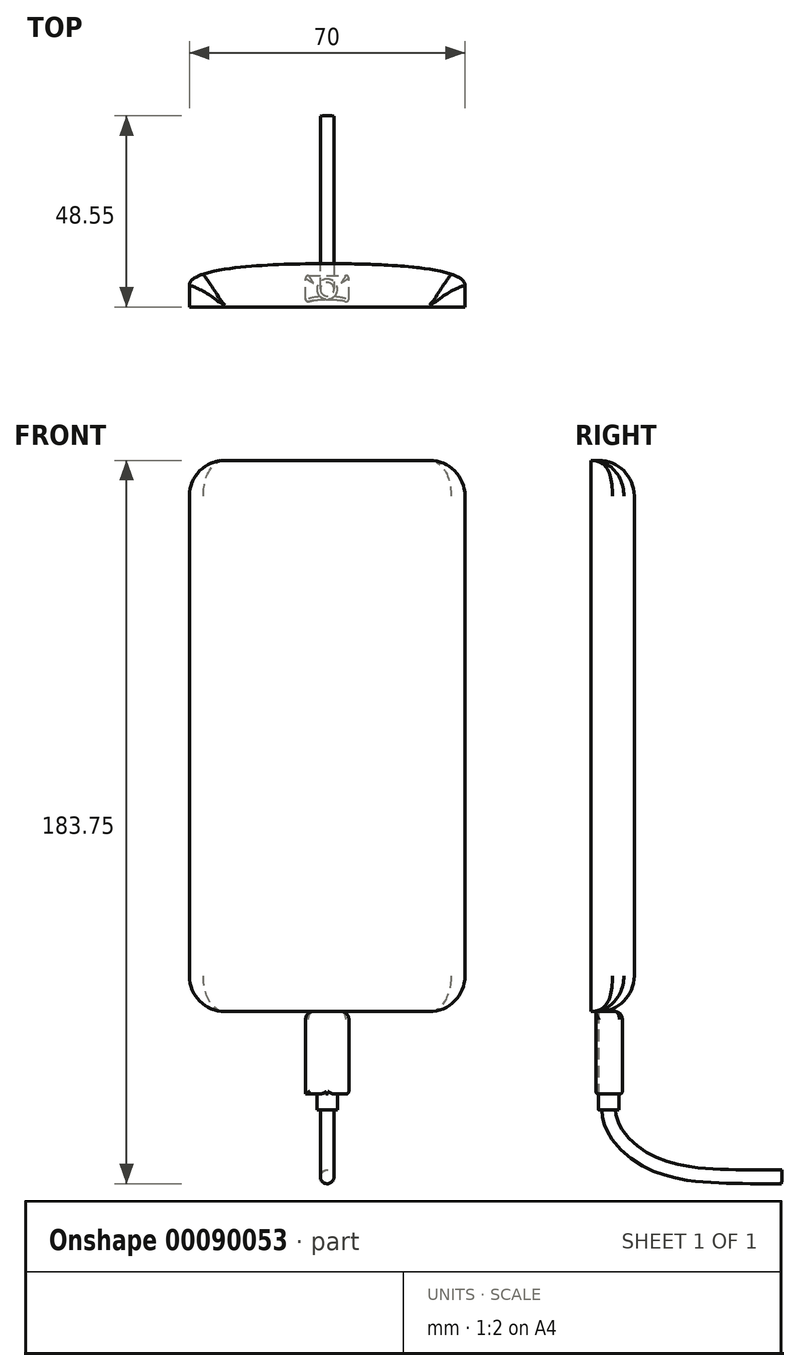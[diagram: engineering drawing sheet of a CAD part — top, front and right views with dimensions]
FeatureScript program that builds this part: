
annotation { "Feature Type Name" : "Feature", "Feature Type Description" : "" }
export const myFeature = defineFeature(function(context is Context, id is Id, definition is map)
    precondition{}
    {
        {
            var Q0;
            Q0=qCreatedBy(makeId("Front.planeOp"),FACE);
            var sketch = newSketch(context, id + "F0", { "sketchPlane" : qUnion([Q0])});
            skLineSegment(sketch, "E0.bottom", {"start": v(-35, 140) * mm, "end": v(35, 140) * mm});
            skLineSegment(sketch, "E0.top", {"start": v(-35, 0) * mm, "end": v(35, 0) * mm});
            skLineSegment(sketch, "E0.left", {"start": v(-35, 140) * mm, "end": v(-35, 0) * mm});
            skLineSegment(sketch, "E0.right", {"start": v(35, 140) * mm, "end": v(35, 0) * mm});
            skSolve(sketch);
        }
        {
            var Q0;
            Q0=qSketchRegion(id+"F0",true);
            extrude(context, id + "F1", {"entities" : qUnion([Q0]), "depth" : 11 * mm});
        }
        {
            var Q0;
            Q0=makeQuery(id+"F1.opExtrude","SWEPT_FACE",FACE,{"disambiguationData":[OSD([sQuery(id+"F0.wireOp",EDGE,"E0.bottom")])]});
            var sketch = newSketch(context, id + "F2", { "sketchPlane" : qUnion([Q0])});
            skFitSpline(sketch, "E1", {"points": [v(-35, -5.5) * mm, v(0, 0) * mm], "startDerivative": vector(0, 16.5) * mm, "endDerivative": vector(18.96, 0) * mm});
            skFitSpline(sketch, "E2.MirrorCS", {"points": [v(35, -5.5) * mm, v(0, 0) * mm], "startDerivative": vector(0, 16.5) * mm, "endDerivative": vector(-18.96, 0) * mm});
            skLineSegment(sketch, "E3", {"start": v(-35, -5.5) * mm, "end": v(-35, 11.17) * mm});
            skLineSegment(sketch, "E4", {"start": v(35, -5.5) * mm, "end": v(35, 11.17) * mm});
            skLineSegment(sketch, "E5", {"start": v(35, 11.17) * mm, "end": v(-35, 11.17) * mm});
            skSolve(sketch);
        }
        {
            var Q0;
            Q0=qSketchRegion(id+"F2",true);
            extrude(context, id + "F3", {"entities" : qUnion([Q0]), "operationType" : NewBodyOperationType.REMOVE, "endBound" : BoundingType.THROUGH_ALL, "oppositeDirection" : true, "depth" : 25 * mm});
        }
        {
            var Q0;
            Q0=makeQuery(id+"F1.opExtrude","SWEPT_EDGE",EDGE,{"disambiguationData":[OSD([sQuery(id+"F0.wireOp",EDGE,"E0.bottom"),sQuery(id+"F0.wireOp",EDGE,"E0.left")])]});
            var Q1;
            Q1=makeQuery(id+"F1.opExtrude","SWEPT_EDGE",EDGE,{"disambiguationData":[OSD([sQuery(id+"F0.wireOp",EDGE,"E0.top"),sQuery(id+"F0.wireOp",EDGE,"E0.left")])]});
            var Q2;
            Q2=makeQuery(id+"F1.opExtrude","SWEPT_EDGE",EDGE,{"disambiguationData":[OSD([sQuery(id+"F0.wireOp",EDGE,"E0.top"),sQuery(id+"F0.wireOp",EDGE,"E0.right")])]});
            var Q3;
            Q3=makeQuery(id+"F1.opExtrude","SWEPT_EDGE",EDGE,{"disambiguationData":[OSD([sQuery(id+"F0.wireOp",EDGE,"E0.bottom"),sQuery(id+"F0.wireOp",EDGE,"E0.right")])]});
            fillet(context, id + "F4", {"entities" : qUnion([Q0, Q1, Q2, Q3]), "radius" : 9 * mm, "tangentPropagation" : true, "allowEdgeOverflow" : false});
        }
        {
            var Q0;
            Q0=qCreatedBy(makeId("Top.planeOp"),FACE);
            var sketch = newSketch(context, id + "F5", { "sketchPlane" : qUnion([Q0])});
            skLineSegment(sketch, "E6.top", {"start": v(-5.5, -3) * mm, "end": v(5.5, -3) * mm});
            skLineSegment(sketch, "E6.left", {"start": v(-5.5, -10) * mm, "end": v(-5.5, -3) * mm});
            skLineSegment(sketch, "E6.right", {"start": v(5.5, -10) * mm, "end": v(5.5, -3) * mm});
            skPoint(sketch, "E7.1.internal.snap0", {"position": v(0, -10) * mm});
            skFitSpline(sketch, "E7", {"points": [v(-5.5, -10) * mm, v(0, -9.09) * mm, v(5.5, -10) * mm], "startDerivative": vector(11, 4.91) * mm, "endDerivative": vector(11, -4.91) * mm});
            skSolve(sketch);
        }
        {
            var Q0;
            Q0=qSketchRegion(id+"F5",true);
            extrude(context, id + "F6", {"entities" : qUnion([Q0]), "oppositeDirection" : true, "depth" : 21 * mm});
        }
        {
            var Q0;
            Q0=makeQuery(id+"F6.opExtrude","CAP_FACE",FACE,{"disambiguationData":[OSD([sQuery(id+"F5.wireOp",EDGE,"E6.top"),sQuery(id+"F5.wireOp",EDGE,"E6.left"),sQuery(id+"F5.wireOp",EDGE,"E6.right"),sQuery(id+"F5.wireOp",EDGE,"E7")])],"isStart":false});
            var sketch = newSketch(context, id + "F7", { "sketchPlane" : qUnion([Q0])});
            skLineSegment(sketch, "E8", {"start": v(5.5, 10) * mm, "end": v(-5.5, 3) * mm, "construction": true});
            skLineSegment(sketch, "E9", {"start": v(-5.5, 10) * mm, "end": v(5.5, 3) * mm, "construction": true});
            skCircle(sketch, "E10", {"center": v(0, 6.5) * mm, "radius": 2.6 * mm});
            skSolve(sketch);
        }
        {
            var Q0;
            Q0=qSketchRegion(id+"F7",true);
            extrude(context, id + "F8", {"entities" : qUnion([Q0]), "operationType" : NewBodyOperationType.ADD, "depth" : 4 * mm});
        }
        {
            var Q0;
            Q0=qCreatedBy(makeId("Right.planeOp"),FACE);
            var sketch = newSketch(context, id + "F9", { "sketchPlane" : qUnion([Q0])});
            skLineSegment(sketch, "E11.bottom", {"start": v(-6.5, -25) * mm, "end": v(37.5, -25) * mm, "construction": true});
            skLineSegment(sketch, "E11.top", {"start": v(-6.5, -42) * mm, "end": v(37.5, -42) * mm, "construction": true});
            skLineSegment(sketch, "E11.left", {"start": v(-6.5, -25) * mm, "end": v(-6.5, -42) * mm, "construction": true});
            skLineSegment(sketch, "E11.right", {"start": v(37.5, -25) * mm, "end": v(37.5, -42) * mm, "construction": true});
            skFitSpline(sketch, "E12", {"points": [v(-6.5, -25) * mm, v(4.01, -38.24) * mm, v(37.5, -42) * mm], "startDerivative": vector(1.17, -39.65) * mm, "endDerivative": vector(78.42, 0) * mm});
            skSolve(sketch);
        }
        {
            var Q0;
            Q0=makeQuery(id+"F8.opExtrude","CAP_FACE",FACE,{"disambiguationData":[OSD([sQuery(id+"F7.wireOp",EDGE,"E10")])],"isStart":false});
            var sketch = newSketch(context, id + "F10", { "sketchPlane" : qUnion([Q0])});
            skCircle(sketch, "E13", {"center": v(0, 6.5) * mm, "radius": 1.75 * mm});
            skSolve(sketch);
        }
        {
            var Q0;
            Q0=makeQuery(id+"F10.imprint","IMPRINT",FACE,{"disambiguationData":[TD([[makeQuery(id+"F10.imprint","IMPRINT",EDGE,{"derivedFrom":sQuery(id+"F10.wireOp",EDGE,"E13")}),1.0]])]});
            var Q1;
            Q1=sQuery(id+"F9.wireOp",EDGE,"E12");
            sweep(context, id + "F11", {"operationType" : NewBodyOperationType.ADD, "profiles" : qUnion([Q0]), "path" : qUnion([Q1])});
        }
        {
            var Q0;
            Q0=makeQuery(id+"F6.opExtrude","SWEPT_EDGE",EDGE,{"disambiguationData":[OSD([sQuery(id+"F5.wireOp",EDGE,"E6.left"),sQuery(id+"F5.wireOp",EDGE,"E7")])]});
            var Q1;
            Q1=makeQuery(id+"F6.opExtrude","SWEPT_EDGE",EDGE,{"disambiguationData":[OSD([sQuery(id+"F5.wireOp",EDGE,"E6.right"),sQuery(id+"F5.wireOp",EDGE,"E7")])]});
            var Q2;
            Q2=makeQuery(id+"F6.opExtrude","SWEPT_EDGE",EDGE,{"disambiguationData":[OSD([sQuery(id+"F5.wireOp",EDGE,"E6.top"),sQuery(id+"F5.wireOp",EDGE,"E6.right")])]});
            var Q3;
            Q3=makeQuery(id+"F6.opExtrude","SWEPT_EDGE",EDGE,{"disambiguationData":[OSD([sQuery(id+"F5.wireOp",EDGE,"E6.top"),sQuery(id+"F5.wireOp",EDGE,"E6.left")])]});
            var Q4;
            Q4=makeQuery(id+"F6.opExtrude","CAP_EDGE",EDGE,{"disambiguationData":[OSD([sQuery(id+"F5.wireOp",EDGE,"E6.right")])],"isStart":false});
            var Q5;
            {var subQ0=sQuery(id+"F5.wireOp",EDGE,"E7");var subQ1=sQuery(id+"F7.wireOp",EDGE,"E10");var subQ2=sQuery(id+"F5.wireOp",EDGE,"E6.right");Q5=makeQuery(id+"F8.boolean.opBoolean","SPLIT",EDGE,{"disambiguationData":[TD([makeQuery(id+"F6.opExtrude","CAP_FACE",FACE,{"disambiguationData":[OSD([sQuery(id+"F5.wireOp",EDGE,"E6.top"),sQuery(id+"F5.wireOp",EDGE,"E6.left"),subQ2,subQ0])],"isStart":false}),makeQuery(id+"F6.opExtrude","SWEPT_FACE",FACE,{"disambiguationData":[OSD([subQ2])]}),makeQuery(id+"F6.opExtrude","SWEPT_FACE",FACE,{"disambiguationData":[OSD([subQ0])]}),makeQuery(id+"F8.opExtrude","SWEPT_FACE",FACE,{"disambiguationData":[OSD([subQ1])]}),makeQuery(id+"F8.opExtrude","CAP_FACE",FACE,{"disambiguationData":[OSD([subQ1])],"isStart":true})])],"derivedFrom":makeQuery(id+"F6.opExtrude","CAP_EDGE",EDGE,{"disambiguationData":[OSD([subQ0])],"isStart":false})});}
            var Q6;
            {var subQ0=sQuery(id+"F5.wireOp",EDGE,"E7");var subQ1=sQuery(id+"F7.wireOp",EDGE,"E10");var subQ2=sQuery(id+"F5.wireOp",EDGE,"E6.left");Q6=makeQuery(id+"F8.boolean.opBoolean","SPLIT",EDGE,{"disambiguationData":[TD([makeQuery(id+"F6.opExtrude","CAP_FACE",FACE,{"disambiguationData":[OSD([sQuery(id+"F5.wireOp",EDGE,"E6.top"),subQ2,sQuery(id+"F5.wireOp",EDGE,"E6.right"),subQ0])],"isStart":false}),makeQuery(id+"F6.opExtrude","SWEPT_FACE",FACE,{"disambiguationData":[OSD([subQ2])]}),makeQuery(id+"F6.opExtrude","SWEPT_FACE",FACE,{"disambiguationData":[OSD([subQ0])]}),makeQuery(id+"F8.opExtrude","SWEPT_FACE",FACE,{"disambiguationData":[OSD([subQ1])]}),makeQuery(id+"F8.opExtrude","CAP_FACE",FACE,{"disambiguationData":[OSD([subQ1])],"isStart":true})])],"derivedFrom":makeQuery(id+"F6.opExtrude","CAP_EDGE",EDGE,{"disambiguationData":[OSD([subQ0])],"isStart":false})});}
            var Q7;
            Q7=makeQuery(id+"F6.opExtrude","CAP_EDGE",EDGE,{"disambiguationData":[OSD([sQuery(id+"F5.wireOp",EDGE,"E6.top")])],"isStart":false});
            fillet(context, id + "F12", {"entities" : qUnion([Q0, Q1, Q2, Q3, Q4, Q5, Q6, Q7]), "radius" : 0.75 * mm, "tangentPropagation" : true, "allowEdgeOverflow" : false});
        }
        {
            var Q0;
            Q0=makeQuery(id+"F6.opExtrude","CAP_EDGE",EDGE,{"disambiguationData":[OSD([sQuery(id+"F5.wireOp",EDGE,"E6.top")])],"isStart":true});
            var Q1;
            Q1=makeQuery(id+"F6.opExtrude","CAP_EDGE",EDGE,{"disambiguationData":[OSD([sQuery(id+"F5.wireOp",EDGE,"E6.right")])],"isStart":true});
            var Q2;
            Q2=makeQuery(id+"F6.opExtrude","CAP_EDGE",EDGE,{"disambiguationData":[OSD([sQuery(id+"F5.wireOp",EDGE,"E6.left")])],"isStart":true});
            fillet(context, id + "F13", {"entities" : qUnion([Q0, Q1, Q2]), "radius" : 2 * mm, "allowEdgeOverflow" : false});
        }
    });
